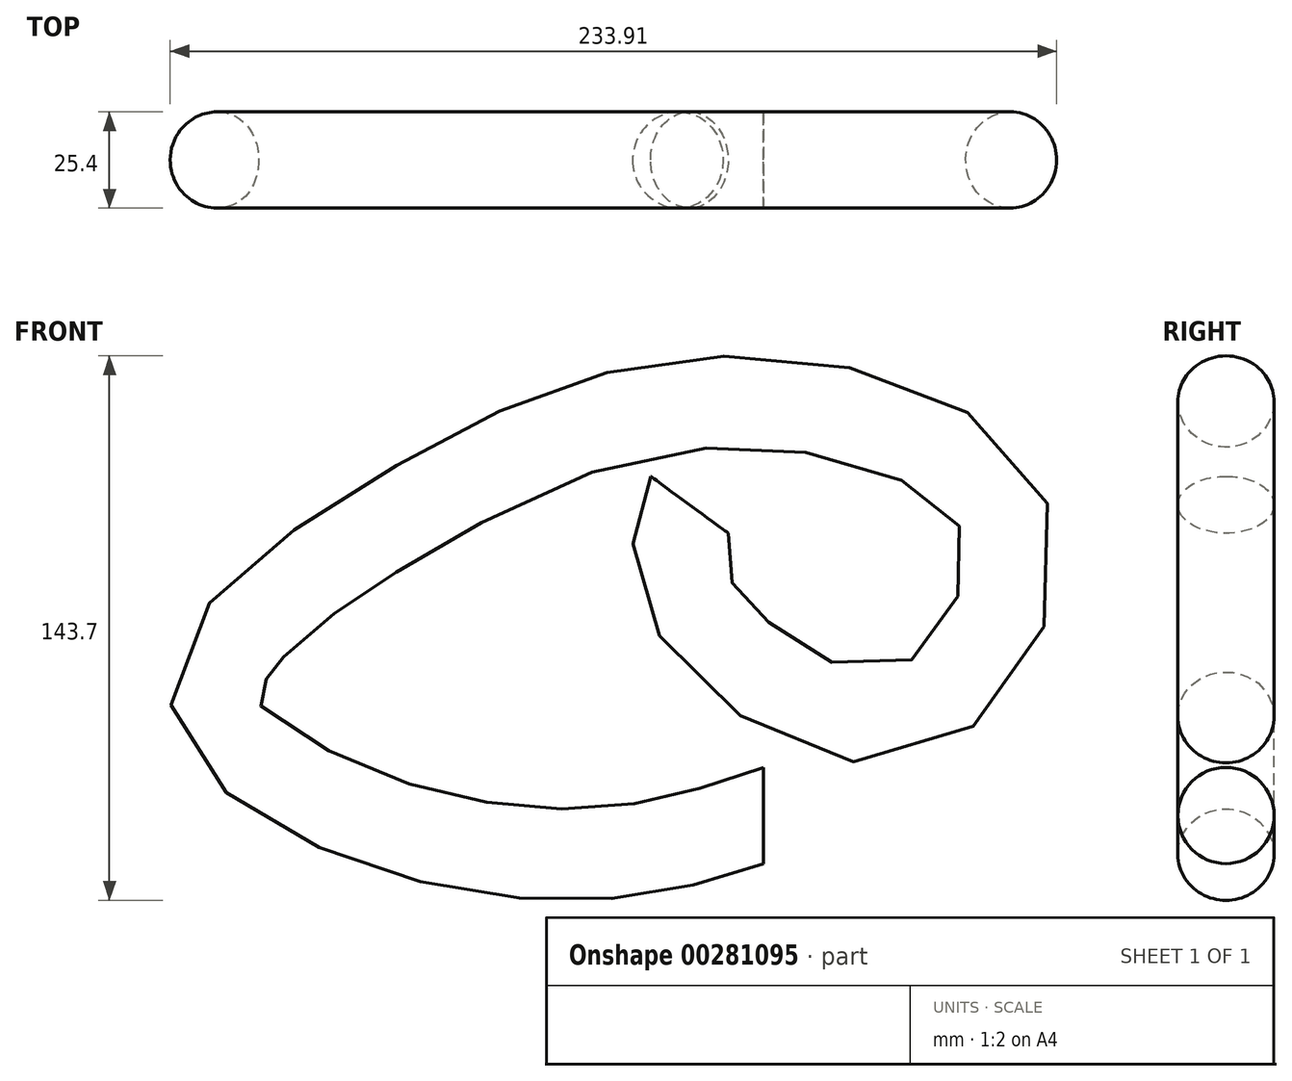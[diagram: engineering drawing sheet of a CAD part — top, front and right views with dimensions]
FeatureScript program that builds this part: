
annotation { "Feature Type Name" : "Feature", "Feature Type Description" : "" }
export const myFeature = defineFeature(function(context is Context, id is Id, definition is map)
    precondition{}
    {
        {
            var Q0;
            Q0=qCreatedBy(makeId("Front.planeOp"),FACE);
            var sketch = newSketch(context, id + "F0", { "sketchPlane" : qUnion([Q0])});
            skFitSpline(sketch, "E0", {"points": [v(0, 0) * mm, v(-40.91, -9.84) * mm, v(-105.9, 0) * mm, v(-144.23, 32.63) * mm, v(-92.96, 80.66) * mm, v(-7.31, 109.2) * mm, v(63.83, 77.03) * mm, v(34.83, 26.73) * mm, v(-19.55, 58) * mm, v(-19.55, 82.02) * mm], "startDerivative": vector(-406.18, -135.57) * mm, "endDerivative": vector(99.26, 308.56) * mm});
            skSolve(sketch);
        }
        {
            var Q0;
            Q0=qCreatedBy(makeId("Right.planeOp"),FACE);
            var sketch = newSketch(context, id + "F1", { "sketchPlane" : qUnion([Q0])});
            skCircle(sketch, "E1", {"center": v(0, 0) * mm, "radius": 12.7 * mm});
            skSolve(sketch);
        }
        {
            var Q0;
            Q0=makeQuery(id+"F1.imprint","IMPRINT",FACE,{"disambiguationData":[TD([[makeQuery(id+"F1.imprint","IMPRINT",EDGE,{"derivedFrom":sQuery(id+"F1.wireOp",EDGE,"E1")}),1.0]])]});
            var Q1;
            Q1=sQuery(id+"F0.wireOp",EDGE,"E0");
            sweep(context, id + "F2", {"profiles" : qUnion([Q0]), "path" : qUnion([Q1])});
        }
    });
